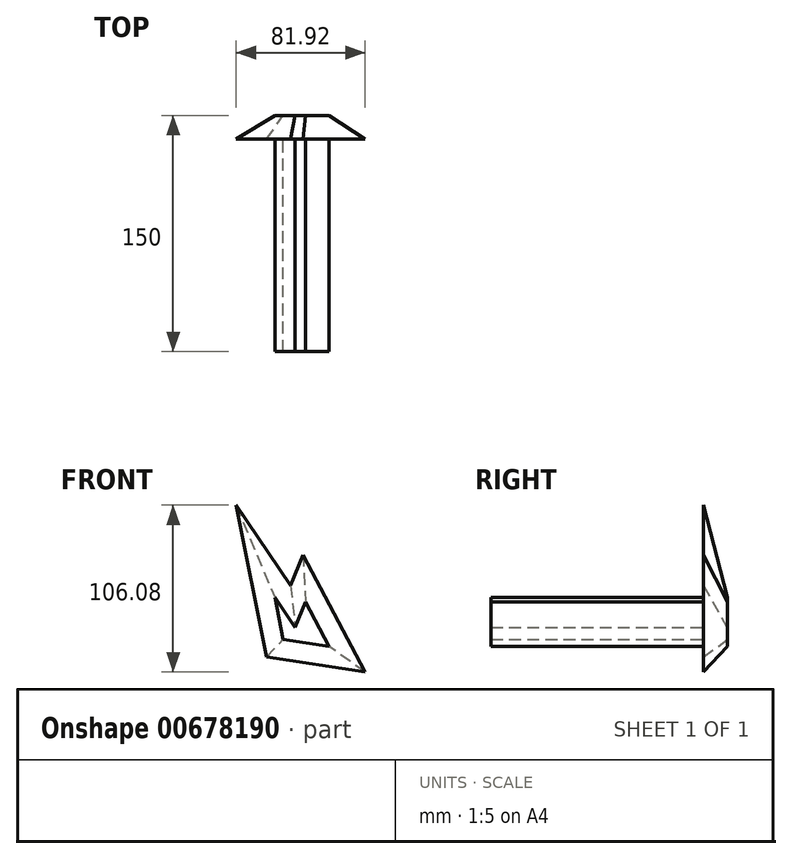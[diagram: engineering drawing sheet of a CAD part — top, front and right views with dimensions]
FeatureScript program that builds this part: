
annotation { "Feature Type Name" : "Feature", "Feature Type Description" : "" }
export const myFeature = defineFeature(function(context is Context, id is Id, definition is map)
    precondition{}
    {
        {
            var Q0;
            Q0=qCreatedBy(makeId("Front.planeOp"),FACE);
            var sketch = newSketch(context, id + "F0", { "sketchPlane" : qUnion([Q0])});
            skLineSegment(sketch, "E0", {"start": v(-14.45, 15.92) * mm, "end": v(-1.5, -3.2) * mm});
            skLineSegment(sketch, "E1", {"start": v(-1.5, -3.2) * mm, "end": v(5.03, 13.14) * mm});
            skLineSegment(sketch, "E2", {"start": v(5.03, 13.14) * mm, "end": v(20.04, -15.17) * mm});
            skLineSegment(sketch, "E3", {"start": v(20.04, -15.17) * mm, "end": v(-9.12, -10.7) * mm});
            skLineSegment(sketch, "E4", {"start": v(-9.12, -10.7) * mm, "end": v(-14.45, 15.92) * mm});
            skSolve(sketch);
        }
        {
            var Q0;
            Q0 = qSketchRegion(id + "F0", true);
            extrude(context, id + "F1", {"entities" : qUnion([Q0]), "depth" : 150 * mm, "offsetDistance" : 25 * mm});
        }
        {
            var Q0;
            Q0 = qSketchRegion(id + "F0", true);
            extrude(context, id + "F2", {"entities" : qUnion([Q0]), "operationType" : NewBodyOperationType.ADD, "depth" : 15 * mm, "offsetDistance" : 25 * mm, "hasDraft" : true, "draftAngle" : 40 * degree});
        }
    });
